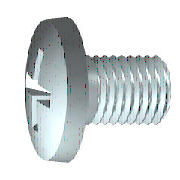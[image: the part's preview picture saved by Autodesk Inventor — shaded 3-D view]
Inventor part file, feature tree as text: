
AUTODESK INVENTOR PART (.ipt)
format: ipt  version: 2015 (Build 190159000, 159)  size: 248,832 bytes
history: native  units: mm (DEFAULTED — no unit token found)
features: chamfer x4, other x3, sketch x2, revolve x1, fillet x1, extrude x1, pattern_circular x1
ambient origin geometry x8: Origin, YZ Plane, XZ Plane, XY Plane, X Axis, Y Axis, Z Axis, Center Point
bodies: Solid1 (feature_tree)
feature tree (13):
  revolve  "Revolution1"  [1 undecoded]
  chamfer  "Chamfer1"  Distance=0.15mm
  chamfer  "Chamfer2"  Distance=0.15mm
  fillet  "Fillet1"  Radius=0.3mm
  extrude  "Extrusion1"  Depth=10.0mm
  pattern_circular  "PolarArray1"  [2 undecoded]
  chamfer  "Chamfer3"  Distance=2.184mm
  chamfer  "Chamfer4"  Distance=0.84mm
  other  "MSC_A1"
  other  "MSC_PF1"
  other  "MSC_PT1"
  sketch  "Sketch2"  dims[d6=3.2mm d9=0.872665mm]
  sketch  "Sketch3"  dims[d10=90.0deg d11=0.15mm d12=0.15mm d13=0.3mm d14=0.3mm d16=10.0mm d17=0.0mm d19=2.184mm d20=0.84mm d21=2.82mm d22=0.7mm d23=0.0mm d24=40.0mm d26=360.0deg d28=0.0mm d29=0.0mm d30=0.6mm d31=0.6mm d32=0.28mm d33=0.28mm d34=45.0deg d35=45.0deg d36=45.0deg d37=45.0deg d38=0.0mm d39=0.0mm d40=0.0mm]
note: 3 required parameter values undecoded (feature->parameter linkage not recoverable at this tier; creation-order binding heuristic only, values carry confidence <= 0.55)